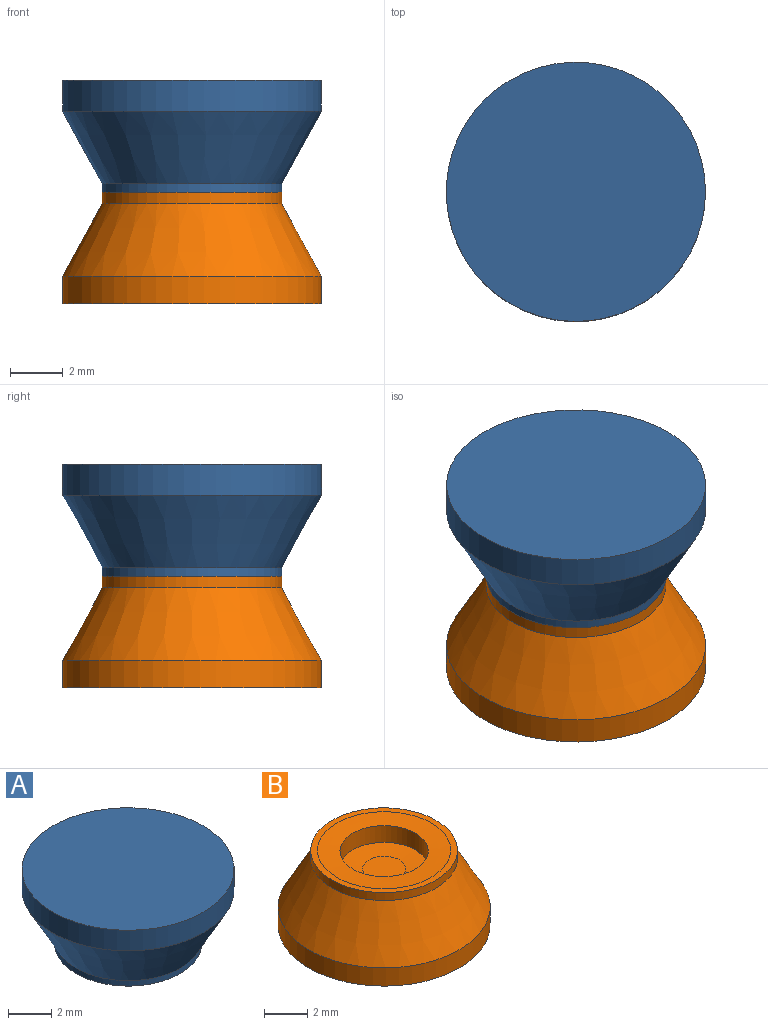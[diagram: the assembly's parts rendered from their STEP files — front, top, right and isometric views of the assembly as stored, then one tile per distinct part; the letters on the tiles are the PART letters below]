
ASSEMBLY  parts=2 mates=1
PART A: 7 faces, bbox 9.9x9.9x5.3 mm
  f0: cylinder r=3.41mm len=6.83mm, axis (0,0,1), area 6.6mm2, adj f1,f6
  f1: plane 6.83x6.83mm, normal (0,0,-1), area 24mm2, adj f0,f2
  f2: cylinder r=2mm len=4mm, axis (0,0,1), area 12.6mm2, adj f1,f3
  f3: plane 4x4mm, normal (0,0,-1), area 12.6mm2, adj f2
  f4: plane 9.86x9.86mm, normal (0,0,1), area 76.4mm2, adj f5
  f5: cylinder r=4.93mm len=9.86mm, axis (0,0,1), area 36.4mm2, adj f4,f6
  f6: cone r=3.41mm half-angle=28.8deg, axis (0,0,1), area 82.6mm2, adj f0,f5
PART B: 9 faces, bbox 9.9x9.9x4.3 mm
  f0: plane 2x2mm, normal (0,0,1), area 3.1mm2, adj f8
  f1: cylinder r=2.05mm len=4.1mm, axis (0,0,1), area 12.2mm2, adj f7,f8
  f2: plane 6.83x6.83mm, normal (0,0,1), area 6.4mm2, adj f3,f7
  f3: cylinder r=3.41mm len=6.83mm, axis (0,0,1), area 9.6mm2, adj f2,f4
  f4: cone r=4.93mm half-angle=28.8deg, axis (0,0,-1), area 82.6mm2, adj f3,f5
  f5: cylinder r=4.93mm len=9.86mm, axis (0,0,1), area 32.1mm2, adj f4,f6
  f6: plane 9.86x9.86mm, normal (0,0,-1), area 76.4mm2, adj f5
  f7: cone r=2.05mm half-angle=87.3deg, axis (0,0,1), area 17mm2, adj f1,f2
  f8: cone r=1mm half-angle=87.3deg, axis (0,0,1), area 10.1mm2, adj f0,f1
PLACE A t=(3.39,1.93,2.04)mm
PLACE B t=(3.39,1.93,2.04)mm
MATE revolute A.f0 <-> B.f1  axis (0,0,-1) through (3.39,1.93,1.04)mm
